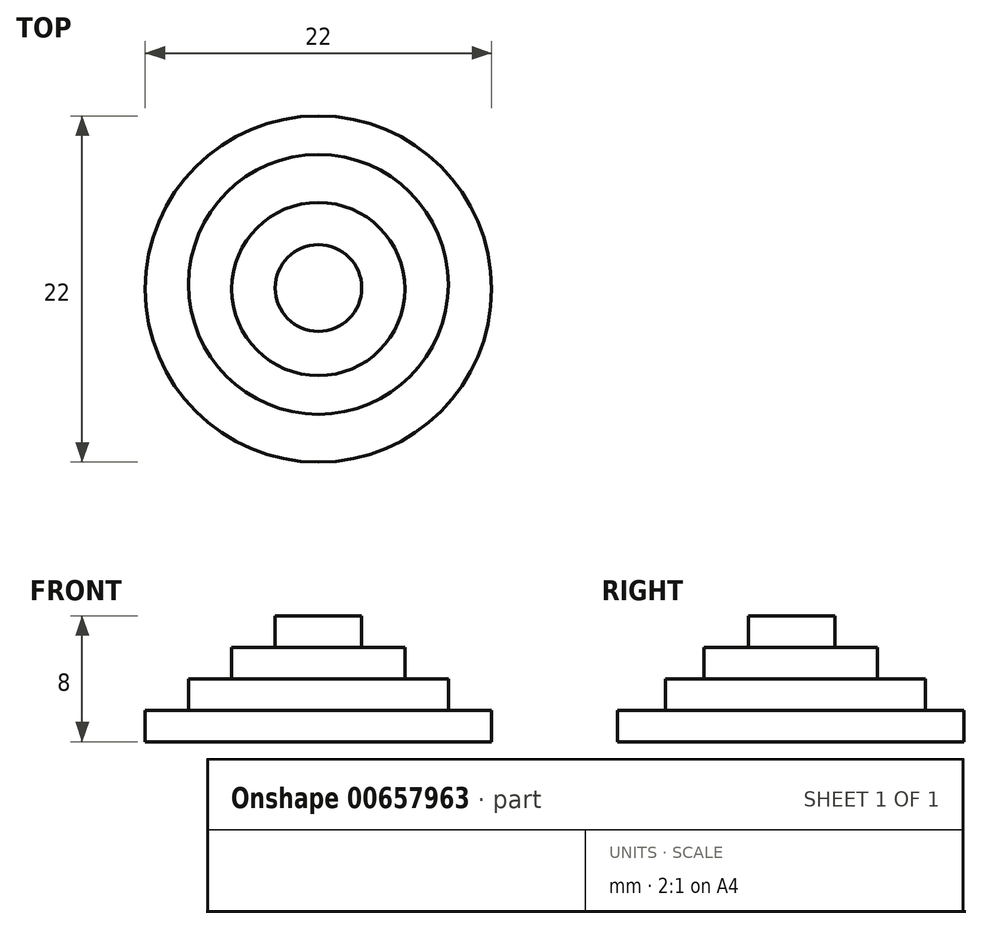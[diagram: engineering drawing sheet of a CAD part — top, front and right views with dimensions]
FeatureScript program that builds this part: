
annotation { "Feature Type Name" : "Feature", "Feature Type Description" : "" }
export const myFeature = defineFeature(function(context is Context, id is Id, definition is map)
    precondition{}
    {
        {
            var Q0;
            Q0=qCreatedBy(makeId("Top.planeOp"),FACE);
            var sketch = newSketch(context, id + "F0", { "sketchPlane" : qUnion([Q0])});
            skCircle(sketch, "E0", {"center": v(0, 0) * mm, "radius": 11 * mm});
            skSolve(sketch);
        }
        {
            var Q0;
            Q0=makeQuery(id+"F0.imprint","IMPRINT",FACE,{"disambiguationData":[TD([[makeQuery(id+"F0.imprint","IMPRINT",EDGE,{"derivedFrom":sQuery(id+"F0.wireOp",EDGE,"E0")}),1.0]])]});
            extrude(context, id + "F1", {"entities" : qUnion([Q0]), "depth" : 2 * mm, "offsetDistance" : 25 * mm});
        }
        {
            var Q0;
            Q0=makeQuery(id+"F1.opExtrude","CAP_FACE",FACE,{"disambiguationData":[OSD([sQuery(id+"F0.wireOp",EDGE,"E0")])],"isStart":false});
            var sketch = newSketch(context, id + "F2", { "sketchPlane" : qUnion([Q0])});
            skCircle(sketch, "E1", {"center": v(0, 0.3) * mm, "radius": 8.25 * mm});
            skSolve(sketch);
        }
        {
            var Q0;
            Q0 = qSketchRegion(id + "F2", true);
            var Q1;
            {var subQ0=sQuery(id+"F2.wireOp",EDGE,"E1");var subQ1=makeQuery(id+"F1.opExtrude","CAP_EDGE",EDGE,{"disambiguationData":[OSD([sQuery(id+"F0.wireOp",EDGE,"E0")])],"isStart":false});var subQ2=makeQuery(id+"F2.imprint","INTERSECT",VERTEX,{"disambiguationData":[OD(0.0)],"derivedFrom":[subQ1,subQ0]});Q1=makeQuery(id+"F2.imprint","IMPRINT",FACE,{"disambiguationData":[TD([[makeQuery(id+"F2.imprint","IMPRINT",EDGE,{"disambiguationData":[TD([[subQ2,-1.0]])],"derivedFrom":subQ0}),1.0]])]});}
            extrude(context, id + "F3", {"entities" : qUnion([Q0, Q1]), "operationType" : NewBodyOperationType.ADD, "depth" : 2 * mm, "offsetDistance" : 25 * mm});
        }
        {
            var Q0;
            Q0=makeQuery(id+"F3.opExtrude","CAP_FACE",FACE,{"disambiguationData":[OSD([sQuery(id+"F2.wireOp",EDGE,"E1")])],"isStart":false});
            var sketch = newSketch(context, id + "F4", { "sketchPlane" : qUnion([Q0])});
            skCircle(sketch, "E2", {"center": v(0, 0) * mm, "radius": 5.5 * mm});
            skSolve(sketch);
        }
        {
            var Q0;
            Q0=makeQuery(id+"F4.imprint","IMPRINT",FACE,{"disambiguationData":[TD([[makeQuery(id+"F4.imprint","IMPRINT",EDGE,{"derivedFrom":sQuery(id+"F4.wireOp",EDGE,"E2")}),1.0]])]});
            extrude(context, id + "F5", {"entities" : qUnion([Q0]), "operationType" : NewBodyOperationType.ADD, "depth" : 2 * mm, "offsetDistance" : 25 * mm});
        }
        {
            var Q0;
            Q0=makeQuery(id+"F5.opExtrude","CAP_FACE",FACE,{"disambiguationData":[OSD([sQuery(id+"F4.wireOp",EDGE,"E2")])],"isStart":false});
            var sketch = newSketch(context, id + "F6", { "sketchPlane" : qUnion([Q0])});
            skCircle(sketch, "E3", {"center": v(0, 0.07) * mm, "radius": 2.75 * mm});
            skSolve(sketch);
        }
        {
            var Q0;
            Q0=makeQuery(id+"F6.imprint","IMPRINT",FACE,{"disambiguationData":[TD([[makeQuery(id+"F6.imprint","IMPRINT",EDGE,{"derivedFrom":sQuery(id+"F6.wireOp",EDGE,"E3")}),1.0]])]});
            extrude(context, id + "F7", {"entities" : qUnion([Q0]), "operationType" : NewBodyOperationType.ADD, "depth" : 2 * mm, "offsetDistance" : 25 * mm});
        }
    });
